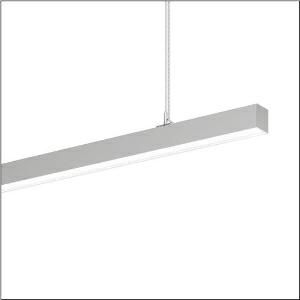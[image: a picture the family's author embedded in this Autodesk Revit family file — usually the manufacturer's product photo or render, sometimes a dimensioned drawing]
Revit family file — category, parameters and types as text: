
# Revit family: silica_r__21_51mx30db45sb_ca73
name_source: partatom
category: Lighting Fixtures
units: mm (PartAtom-declared; Revit-internal decimal feet)

## family parameters
Cut with Voids When Loaded = No
Host = Face
Light Source = No
Part Type = Normal
Room Calculation Point = No
Round Connector Dimension = Use Diameter
Shared = No

## types (1)
- --- (1 x LED, 5260 lm, 32 W, 4000K)
    Apparent Load = 32 VA
    CIE Flux Codes = 47 79 96 57 100
    Color Rendering = 80
    Color Temperature = 4000K
    Default Elevation = 1800 mm
    Description = Silica® 21, office luminaire, primary optical cover: cover, of PMMA, opal, light emission: direct/indirect distribution, primary light characteristic: symmetric, installation type: suspended mounting, LED, rated luminous flux: 5.260lm, luminous efficacy: 164lm/W, light colour: 840, colour temperature: 4000K, with terminal, 3+2-pole, max. 2.5mm², mains connection: 220..240V, AC, 50/60Hz, rated input power: 32W, luminaire housing, of aluminium, metallic grey (RAL 9006), length: 1.504mm, width: 53mm, height: 53mm, protection rating (complete): IP20, insulation class (complete): insulation class I (protective earthing), certification: CE, permissible operating ambient temperature: 0..+35°C, standard: EN 50419, packaging unit: 1 piece
    Height = 53 mm
    Lamp = 1 x LED
    Lamp Light Flux = 5260 lm
    Lamp Power = 32 W
    Lamp count = 1
    Length = 1504 mm
    Luminous efficacy = 164 lm/W
    Manufacturer = Siteco
    ModVariant = No
    Model = 51MX30DB45SB
    Mounting Place = Ceiling
    Mounting Type = Pendant
    Number of Poles = 1
    OnlyDefault = Yes
    Power Factor = 1
    Product Name = Silica® 21
    Product group = office luminaire | ceiling pendant
    ProductGroupID = 902
    Protection Class = Protection class I
    Protection Degree = IP 20
    RLX_Detail_Level = 1
    RLX_Emergency_Light_Flux = 0 lm
    RLX_Emergency_Type = 0
    RLX_Emergency_Type_DB = No
    RlxData = <blob elided: 23353 chars, md5=02edbab8>
    Socket = socket
    Standby Power = 0 W
    System Light Flux = 5260 lm
    System Power = 32 W
    Type Comments = factory setting: luminous flux: 100 % | dim-lin: 254 | 218 mA
    Type Image = l_1297747.jpg
    URL = http://relux.com
    VarID = @adj_046975
    Voltage = 0 V
    Weight = 0.00 kg
    Width = 53 mm

## geometry (parser evidence)
native form markers: Blend x4, Sweep x15
no freeform markers — native parametric forms only
